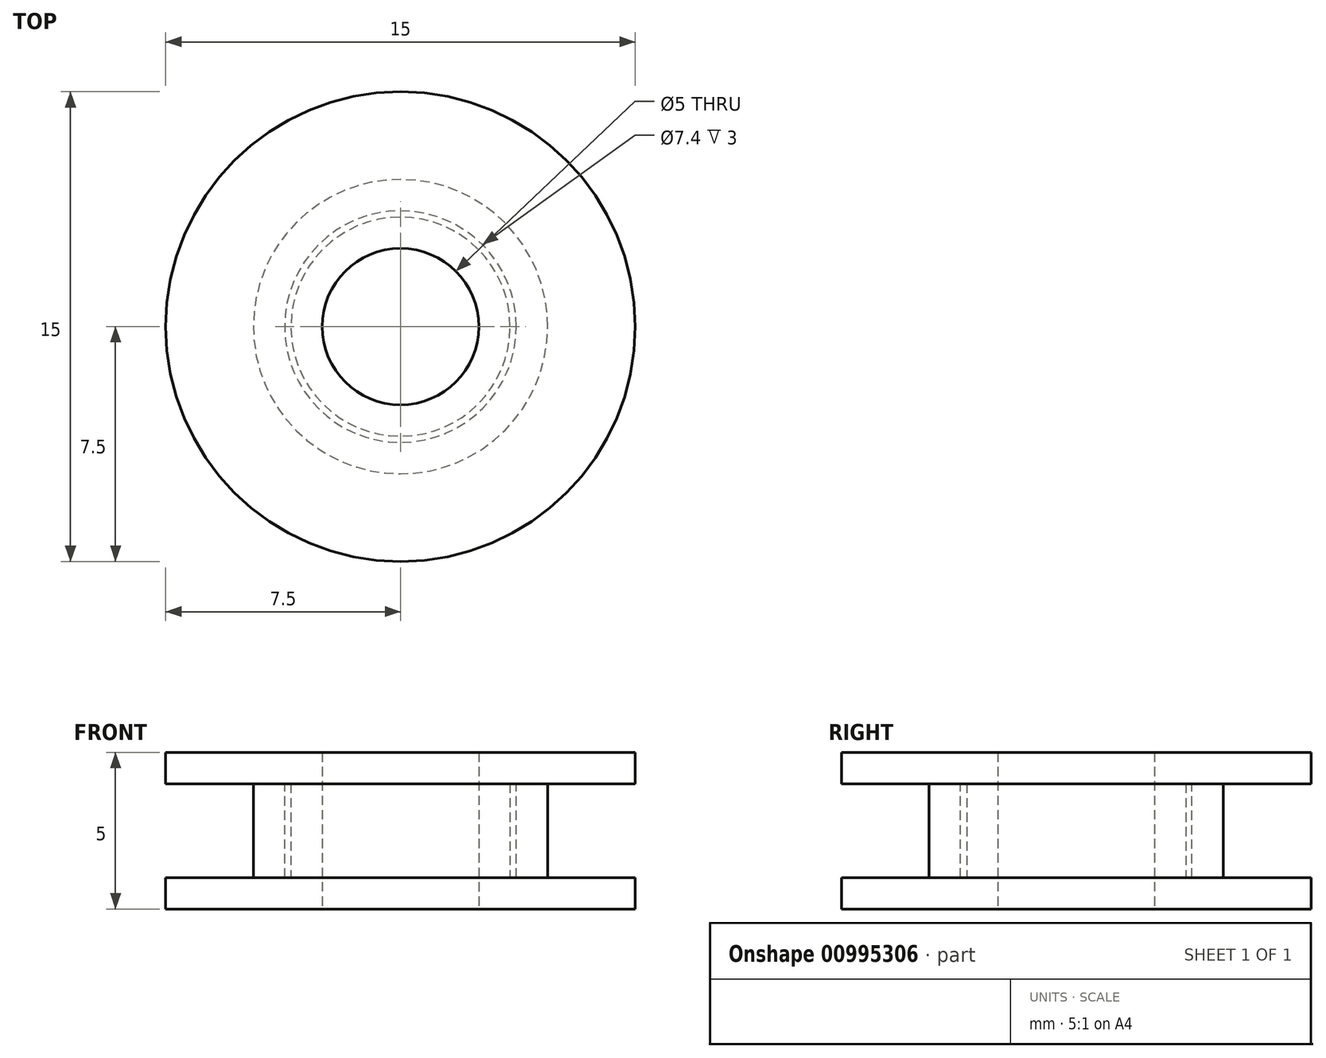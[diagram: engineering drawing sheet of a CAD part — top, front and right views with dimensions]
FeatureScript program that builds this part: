
annotation { "Feature Type Name" : "Feature", "Feature Type Description" : "" }
export const myFeature = defineFeature(function(context is Context, id is Id, definition is map)
    precondition{}
    {
        {
            var Q0;
            Q0=qCreatedBy(makeId("Top.planeOp"),FACE);
            var sketch = newSketch(context, id + "F0", { "sketchPlane" : qUnion([Q0])});
            skCircle(sketch, "E0", {"center": v(0, 0) * mm, "radius": 2.5 * mm});
            skCircle(sketch, "E1", {"center": v(0, 0) * mm, "radius": 7.5 * mm});
            skCircle(sketch, "E2", {"center": v(0, 0) * mm, "radius": 3.5 * mm});
            skSolve(sketch);
        }
        {
            var Q0;
            Q0=makeQuery(id+"F0.imprint","IMPRINT",FACE,{"disambiguationData":[TD([[makeQuery(id+"F0.imprint","IMPRINT",EDGE,{"derivedFrom":sQuery(id+"F0.wireOp",EDGE,"E1")}),1.0]])]});
            var Q1;
            Q1=makeQuery(id+"F0.imprint","IMPRINT",FACE,{"disambiguationData":[TD([[makeQuery(id+"F0.imprint","IMPRINT",EDGE,{"derivedFrom":sQuery(id+"F0.wireOp",EDGE,"E0")}),-1.0]])]});
            extrude(context, id + "F1", {"entities" : qUnion([Q0, Q1]), "depth" : 1 * mm, "offsetDistance" : 25 * mm});
        }
        {
            var Q0;
            Q0=makeQuery(id+"F1.opExtrude","CAP_FACE",FACE,{"disambiguationData":[OSD([sQuery(id+"F0.wireOp",EDGE,"E0"),sQuery(id+"F0.wireOp",EDGE,"E1")])],"isStart":false});
            var sketch = newSketch(context, id + "F2", { "sketchPlane" : qUnion([Q0])});
            skCircle(sketch, "E3.0", {"center": v(0, 0) * mm, "radius": 3.5 * mm});
            skSolve(sketch);
        }
        {
            var Q0;
            Q0=makeQuery(id+"F2.imprint","IMPRINT",FACE,{"disambiguationData":[TD([[makeQuery(id+"F2.imprint","IMPRINT",EDGE,{"derivedFrom":sQuery(id+"F2.wireOp",EDGE,"E3.0")}),1.0]])]});
            extrude(context, id + "F3", {"entities" : qUnion([Q0]), "operationType" : NewBodyOperationType.ADD, "depth" : 3 * mm, "offsetDistance" : 25 * mm});
        }
        {
            var Q0;
            Q0=makeQuery(id+"F3.opExtrude","CAP_FACE",FACE,{"disambiguationData":[OSD([sQuery(id+"F0.wireOp",EDGE,"E0"),sQuery(id+"F2.wireOp",EDGE,"E3.0")])],"isStart":false});
            var sketch = newSketch(context, id + "F4", { "sketchPlane" : qUnion([Q0])});
            skCircle(sketch, "E4.0", {"center": v(0, 0) * mm, "radius": 3.5 * mm});
            skCircle(sketch, "E5.0", {"center": v(0, 0) * mm, "radius": 2.5 * mm});
            skCircle(sketch, "E6.0", {"center": v(0, 0) * mm, "radius": 3.7 * mm});
            skCircle(sketch, "E7.0", {"center": v(0, 0) * mm, "radius": 4.7 * mm});
            skCircle(sketch, "E8.0", {"center": v(0, 0) * mm, "radius": 7.5 * mm});
            skSolve(sketch);
        }
        {
            var Q0;
            Q0=makeQuery(id+"F4.imprint","IMPRINT",FACE,{"disambiguationData":[TD([[makeQuery(id+"F4.imprint","IMPRINT",EDGE,{"derivedFrom":sQuery(id+"F4.wireOp",EDGE,"E6.0")}),-1.0]])]});
            var Q1;
            Q1=makeQuery(id+"F1.opExtrude","CAP_FACE",FACE,{"disambiguationData":[OSD([sQuery(id+"F0.wireOp",EDGE,"E0"),sQuery(id+"F0.wireOp",EDGE,"E1")])],"isStart":false});
            extrude(context, id + "F5", {"entities" : qUnion([Q0]), "endBound" : BoundingType.UP_TO_SURFACE, "oppositeDirection" : true, "depth" : 25 * mm, "endBoundEntityFace" : qUnion([Q1]), "offsetDistance" : 25 * mm});
        }
        {
            var Q0;
            Q0=makeQuery(id+"F4.imprint","IMPRINT",FACE,{"disambiguationData":[TD([[makeQuery(id+"F4.imprint","IMPRINT",EDGE,{"derivedFrom":sQuery(id+"F4.wireOp",EDGE,"E7.0")}),-1.0]])]});
            var Q1;
            Q1=makeQuery(id+"F4.imprint","IMPRINT",FACE,{"disambiguationData":[TD([[makeQuery(id+"F4.imprint","IMPRINT",EDGE,{"derivedFrom":sQuery(id+"F4.wireOp",EDGE,"E6.0")}),-1.0]])]});
            var Q2;
            Q2=makeQuery(id+"F4.imprint","IMPRINT",FACE,{"disambiguationData":[TD([[makeQuery(id+"F4.imprint","IMPRINT",EDGE,{"derivedFrom":sQuery(id+"F4.wireOp",EDGE,"E4.0")}),1.0]])]});
            var Q3;
            Q3=makeQuery(id+"F4.imprint","IMPRINT",FACE,{"disambiguationData":[TD([[makeQuery(id+"F4.imprint","IMPRINT",EDGE,{"derivedFrom":sQuery(id+"F4.wireOp",EDGE,"E4.0")}),-1.0]])]});
            extrude(context, id + "F6", {"entities" : qUnion([Q0, Q1, Q2, Q3]), "operationType" : NewBodyOperationType.ADD, "depth" : 1 * mm, "offsetDistance" : 25 * mm});
        }
    });
